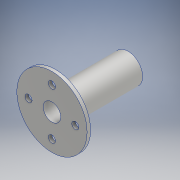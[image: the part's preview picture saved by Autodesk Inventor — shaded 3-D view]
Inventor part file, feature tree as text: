
AUTODESK INVENTOR PART (.ipt)
format: ipt  version: 2018 (Build 220112000, 112)  size: 144,896 bytes
history: native  units: mm
features: sketch x3, extrude x2, other x1, revolve x1, projected_geometry x1
ambient origin geometry x8: Origin, YZ Plane, XZ Plane, XY Plane, X Axis, Y Axis, Z Axis, Center Point
bodies: Body1 (feature_tree)
feature tree (8):
  other  "ソリッド1"
  revolve  "回転1"
  extrude  "押し出し1"  Depth=7.5mm
  extrude  "押し出し2"  Depth=5.0mm
  sketch  "スケッチ1"
  sketch  "スケッチ2"
  sketch  "スケッチ3"
  projected_geometry  "投影ループ1"
